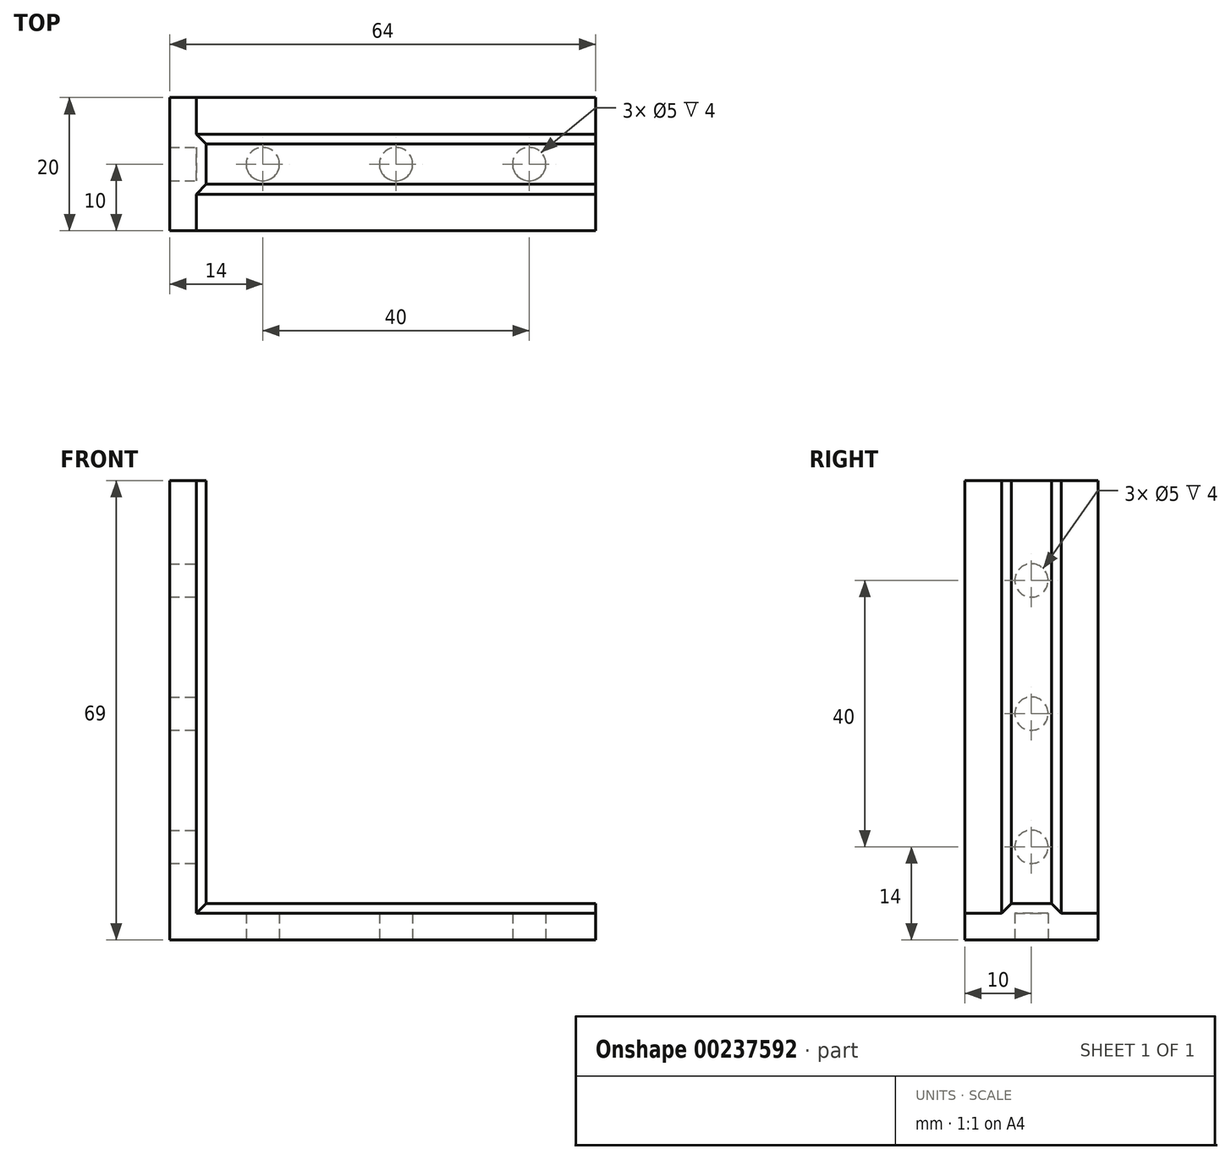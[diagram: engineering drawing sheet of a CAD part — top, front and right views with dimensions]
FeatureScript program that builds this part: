
annotation { "Feature Type Name" : "Feature", "Feature Type Description" : "" }
export const myFeature = defineFeature(function(context is Context, id is Id, definition is map)
    precondition{}
    {
        {
            var Q0;
            Q0=qCreatedBy(makeId("Top.planeOp"),FACE);
            var sketch = newSketch(context, id + "F0", { "sketchPlane" : qUnion([Q0])});
            skLineSegment(sketch, "E0.bottom", {"start": v(0, 0) * mm, "end": v(60, 0) * mm});
            skLineSegment(sketch, "E0.top", {"start": v(0, 20) * mm, "end": v(60, 20) * mm});
            skLineSegment(sketch, "E0.left", {"start": v(0, 0) * mm, "end": v(0, 20) * mm});
            skLineSegment(sketch, "E0.right", {"start": v(60, 0) * mm, "end": v(60, 20) * mm});
            skPoint(sketch, "E1.centerSnap0", {"position": v(0, 10) * mm});
            skCircle(sketch, "E2", {"center": v(10, 10) * mm, "radius": 2.5 * mm});
            skCircle(sketch, "E3", {"center": v(30, 10) * mm, "radius": 2.5 * mm});
            skCircle(sketch, "E4", {"center": v(50, 10) * mm, "radius": 2.5 * mm});
            skSolve(sketch);
        }
        {
            var Q0;
            Q0 = qSketchRegion(id + "F0", true);
            extrude(context, id + "F1", {"entities" : qUnion([Q0]), "depth" : 4 * mm});
        }
        {
            var Q0;
            Q0=qCreatedBy(makeId("Right.planeOp"),FACE);
            var sketch = newSketch(context, id + "F2", { "sketchPlane" : qUnion([Q0])});
            skLineSegment(sketch, "E5.bottom", {"start": v(0, 0) * mm, "end": v(20, 0) * mm});
            skLineSegment(sketch, "E5.top", {"start": v(0, 69) * mm, "end": v(20, 69) * mm});
            skLineSegment(sketch, "E5.left", {"start": v(0, 0) * mm, "end": v(0, 69) * mm});
            skLineSegment(sketch, "E5.right", {"start": v(20, 0) * mm, "end": v(20, 69) * mm});
            skCircle(sketch, "E6", {"center": v(10, 14) * mm, "radius": 2.5 * mm});
            skPoint(sketch, "E6.centerSnap0", {"position": v(10, 0) * mm});
            skCircle(sketch, "E7", {"center": v(10, 34) * mm, "radius": 2.5 * mm});
            skCircle(sketch, "E8", {"center": v(10, 54) * mm, "radius": 2.5 * mm});
            skSolve(sketch);
        }
        {
            var Q0;
            Q0 = qSketchRegion(id + "F2", true);
            extrude(context, id + "F3", {"entities" : qUnion([Q0]), "operationType" : NewBodyOperationType.ADD, "oppositeDirection" : true, "depth" : 4 * mm});
        }
        {
            var Q0;
            Q0=makeQuery(id+"F1.opExtrude","SWEPT_FACE",FACE,{"disambiguationData":[OSD([sQuery(id+"F0.wireOp",EDGE,"E0.right")])]});
            var sketch = newSketch(context, id + "F4", { "sketchPlane" : qUnion([Q0])});
            skLineSegment(sketch, "E9", {"start": v(5.5, 4) * mm, "end": v(7, 5.5) * mm});
            skLineSegment(sketch, "E10", {"start": v(7, 5.5) * mm, "end": v(13, 5.5) * mm});
            skLineSegment(sketch, "E11", {"start": v(13, 5.5) * mm, "end": v(14.5, 4) * mm});
            skLineSegment(sketch, "E12", {"start": v(14.5, 4) * mm, "end": v(5.5, 4) * mm});
            skSolve(sketch);
        }
        {
            var Q0;
            Q0 = qSketchRegion(id + "F4", true);
            var Q1;
            Q1=makeQuery(id+"F3.opExtrude","CAP_FACE",FACE,{"disambiguationData":[OSD([sQuery(id+"F2.wireOp",EDGE,"E5.bottom"),sQuery(id+"F2.wireOp",EDGE,"E5.top"),sQuery(id+"F2.wireOp",EDGE,"E5.left"),sQuery(id+"F2.wireOp",EDGE,"E5.right"),sQuery(id+"F2.wireOp",EDGE,"E6"),sQuery(id+"F2.wireOp",EDGE,"E7"),sQuery(id+"F2.wireOp",EDGE,"E8")])],"isStart":true});
            extrude(context, id + "F5", {"entities" : qUnion([Q0]), "operationType" : NewBodyOperationType.ADD, "endBound" : BoundingType.UP_TO_SURFACE, "oppositeDirection" : true, "endBoundEntityFace" : qUnion([Q1]), "depth" : 25 * mm});
        }
        {
            var Q0;
            Q0=makeQuery(id+"F3.opExtrude","SWEPT_FACE",FACE,{"disambiguationData":[OSD([sQuery(id+"F2.wireOp",EDGE,"E5.top")])]});
            var sketch = newSketch(context, id + "F6", { "sketchPlane" : qUnion([Q0])});
            skLineSegment(sketch, "E13.0", {"start": v(0, 13) * mm, "end": v(60, 13) * mm, "construction": true});
            skLineSegment(sketch, "E14.0", {"start": v(0, 14.5) * mm, "end": v(60, 14.5) * mm, "construction": true});
            skLineSegment(sketch, "E15.0", {"start": v(0, 7) * mm, "end": v(60, 7) * mm, "construction": true});
            skLineSegment(sketch, "E16.0", {"start": v(0, 5.5) * mm, "end": v(60, 5.5) * mm, "construction": true});
            skLineSegment(sketch, "E17", {"start": v(0, 14.5) * mm, "end": v(0, 5.5) * mm});
            skLineSegment(sketch, "E18", {"start": v(1.5, 7) * mm, "end": v(0, 5.5) * mm});
            skLineSegment(sketch, "E19", {"start": v(0, 14.5) * mm, "end": v(1.5, 13) * mm});
            skLineSegment(sketch, "E20", {"start": v(1.5, 13) * mm, "end": v(1.5, 7) * mm});
            skSolve(sketch);
        }
        {
            var Q0;
            Q0 = qSketchRegion(id + "F6", true);
            var Q1;
            {var subQ2=sQuery(id+"F0.wireOp",EDGE,"E0.right");var subQ3=sQuery(id+"F0.wireOp",EDGE,"E0.top");Q1=makeQuery(id+"F5.boolean.opBoolean","SPLIT",FACE,{"disambiguationData":[TD([makeQuery(id+"F1.opExtrude","SWEPT_FACE",FACE,{"disambiguationData":[OSD([subQ3])]})])],"derivedFrom":makeQuery(id+"F1.opExtrude","CAP_FACE",FACE,{"disambiguationData":[OSD([sQuery(id+"F0.wireOp",EDGE,"E0.bottom"),subQ3,sQuery(id+"F0.wireOp",EDGE,"E0.left"),subQ2,sQuery(id+"F0.wireOp",EDGE,"E2"),sQuery(id+"F0.wireOp",EDGE,"E3"),sQuery(id+"F0.wireOp",EDGE,"E4")])],"isStart":false})});}
            extrude(context, id + "F7", {"entities" : qUnion([Q0]), "operationType" : NewBodyOperationType.ADD, "endBound" : BoundingType.UP_TO_SURFACE, "oppositeDirection" : true, "endBoundEntityFace" : qUnion([Q1]), "depth" : 25 * mm});
        }
    });
